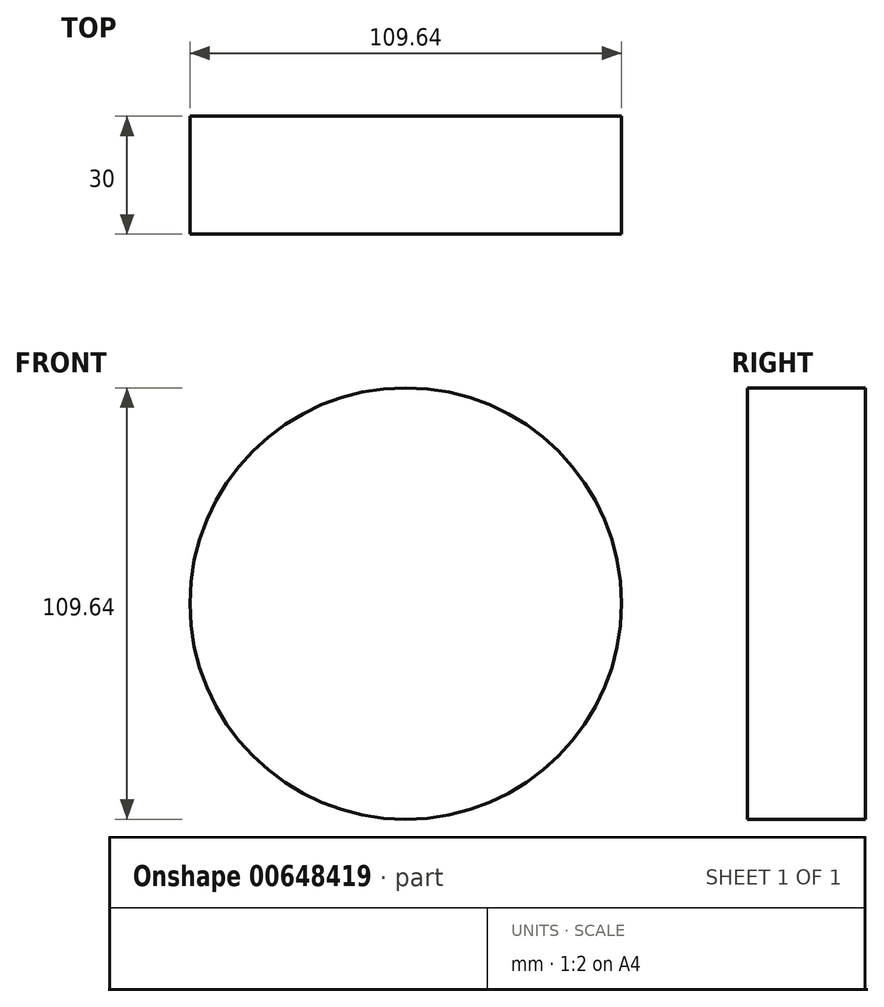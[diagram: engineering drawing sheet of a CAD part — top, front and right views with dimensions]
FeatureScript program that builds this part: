
annotation { "Feature Type Name" : "Feature", "Feature Type Description" : "" }
export const myFeature = defineFeature(function(context is Context, id is Id, definition is map)
    precondition{}
    {
        {
            var Q0;
            Q0=qCreatedBy(makeId("Front.planeOp"),FACE);
            var sketch = newSketch(context, id + "F0", { "sketchPlane" : qUnion([Q0])});
            skCircle(sketch, "E0", {"center": v(0, 0) * mm, "radius": 54.82 * mm});
            skSolve(sketch);
        }
        {
            var Q0;
            Q0=makeQuery(id+"F0.imprint","IMPRINT",FACE,{"disambiguationData":[TD([[makeQuery(id+"F0.imprint","IMPRINT",EDGE,{"derivedFrom":sQuery(id+"F0.wireOp",EDGE,"E0")}),1.0]])]});
            extrude(context, id + "F1", {"entities" : qUnion([Q0]), "depth" : 30 * mm, "offsetDistance" : 25 * mm});
        }
    });
